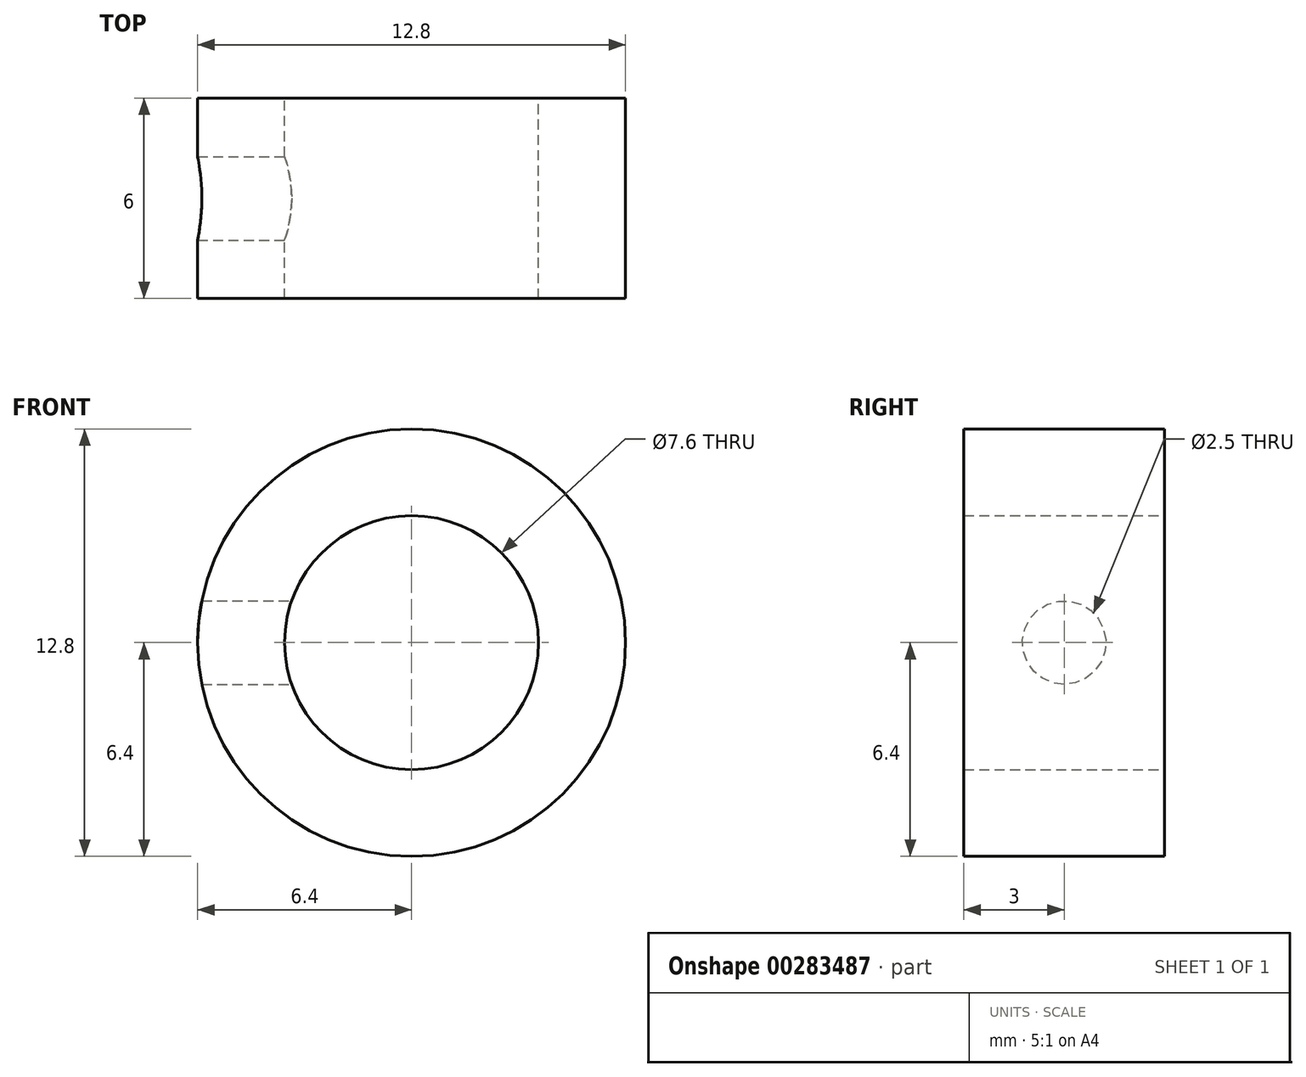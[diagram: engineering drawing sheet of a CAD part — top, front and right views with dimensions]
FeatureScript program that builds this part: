
annotation { "Feature Type Name" : "Feature", "Feature Type Description" : "" }
export const myFeature = defineFeature(function(context is Context, id is Id, definition is map)
    precondition{}
    {
        {
            var Q0;
            Q0=qCreatedBy(makeId("Front.planeOp"),FACE);
            var sketch = newSketch(context, id + "F0", { "sketchPlane" : qUnion([Q0])});
            skCircle(sketch, "E0", {"center": v(0, 0) * mm, "radius": 3.8 * mm});
            skCircle(sketch, "E1.0", {"center": v(0, 0) * mm, "radius": 6.4 * mm});
            skSolve(sketch);
        }
        {
            var Q0;
            Q0=makeQuery(id+"F0.imprint","IMPRINT",FACE,{"disambiguationData":[TD([[makeQuery(id+"F0.imprint","IMPRINT",EDGE,{"derivedFrom":sQuery(id+"F0.wireOp",EDGE,"E0")}),-1.0]])]});
            extrude(context, id + "F1", {"entities" : qUnion([Q0]), "endBound" : BoundingType.SYMMETRIC, "depth" : 6 * mm});
        }
        {
            var Q0;
            Q0=qCreatedBy(makeId("Right.planeOp"),FACE);
            var sketch = newSketch(context, id + "F2", { "sketchPlane" : qUnion([Q0])});
            skCircle(sketch, "E2", {"center": v(0, 0) * mm, "radius": 1.5 * mm});
            skSolve(sketch);
        }
        {
            var Q0;
            Q0=sQuery(id+"F2.wireOp",VERTEX,"E2.center");
            var Q1;
            Q1=makeQuery(id+"F1.opExtrude","SWEPT_BODY",BODY,{"disambiguationData":[OSD([sQuery(id+"F0.wireOp",EDGE,"E0"),sQuery(id+"F0.wireOp",EDGE,"E1.0")])]});
            hole(context, id + "F3", {"style" : HoleStyle.SIMPLE, "endStyle" : HoleEndStyle.THROUGH, "holeDiameter" : 2.5 * mm, "tappedDepth" : 12 * mm, "tapClearance" : 3, "locations" : qUnion([Q0]), "scope" : qUnion([Q1])});
        }
    });
